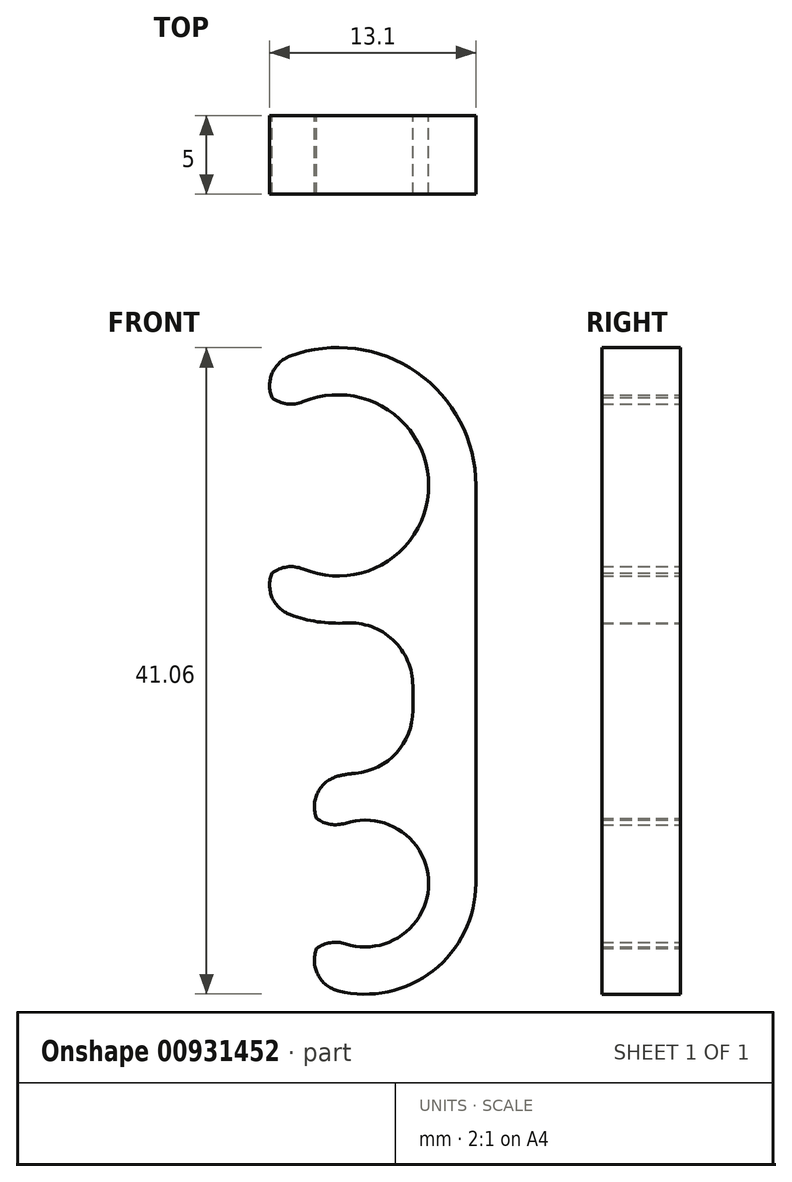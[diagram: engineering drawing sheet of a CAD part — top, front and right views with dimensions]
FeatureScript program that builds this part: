
annotation { "Feature Type Name" : "Feature", "Feature Type Description" : "" }
export const myFeature = defineFeature(function(context is Context, id is Id, definition is map)
    precondition{}
    {
        {
            var Q0;
            Q0=qCreatedBy(makeId("Front.planeOp"),FACE);
            var sketch = newSketch(context, id + "F0", { "sketchPlane" : qUnion([Q0])});
            skPoint(sketch, "E0", {"position": v(5.76, 0) * mm});
            skPoint(sketch, "E1", {"position": v(5.76, -25.29) * mm});
            skLineSegment(sketch, "E2", {"start": v(8.75, 0) * mm, "end": v(8.75, -25.29) * mm});
            skArc(sketch, "E3", {"start": v(-3.18, -8.16) * mm, "mid": v(-1.36, -8.65) * mm, "end": v(0.52, -8.74) * mm});
            skArc(sketch, "E4", {"start": v(-0.29, 8.75) * mm, "mid": v(-8.63, 1.48) * mm, "end": v(-3.18, -8.16) * mm});
            skArc(sketch, "E5", {"start": v(-2.55, -19.7) * mm, "mid": v(-5, -27.33) * mm, "end": v(1.27, -32.3) * mm});
            skArc(sketch, "E6", {"start": v(1.27, -32.3) * mm, "mid": v(8.53, -27.06) * mm, "end": v(4.75, -18.94) * mm});
            skLineSegment(sketch, "E7", {"start": v(-5.33, -6.95) * mm, "end": v(0, 0) * mm});
            skLineSegment(sketch, "E8", {"start": v(0, 0) * mm, "end": v(-5.33, 6.95) * mm});
            skLineSegment(sketch, "E9", {"start": v(1.73, -25.29) * mm, "end": v(-2.55, -19.7) * mm});
            skLineSegment(sketch, "E10", {"start": v(1.73, -25.29) * mm, "end": v(-2.55, -30.86) * mm});
            skArc(sketch, "E11", {"start": v(-3.5, 4.57) * mm, "mid": v(-5.76, 0) * mm, "end": v(-3.5, -4.57) * mm});
            skArc(sketch, "E12", {"start": v(-3.5, -4.57) * mm, "mid": v(5.76, 0) * mm, "end": v(-3.5, 4.57) * mm});
            skArc(sketch, "E13", {"start": v(-0.73, -22.09) * mm, "mid": v(-2.3, -25.29) * mm, "end": v(-0.73, -28.48) * mm});
            skArc(sketch, "E14", {"start": v(-0.73, -28.48) * mm, "mid": v(5.76, -25.29) * mm, "end": v(-0.73, -22.09) * mm});
            skLineSegment(sketch, "E15", {"start": v(1.73, -21.26) * mm, "end": v(-24.2, -21.26) * mm, "construction": true});
            skLineSegment(sketch, "E16", {"start": v(0, -5.75) * mm, "end": v(-23.66, -5.76) * mm, "construction": true});
            skLineSegment(sketch, "E17", {"start": v(4.75, -14.3) * mm, "end": v(4.75, -12.73) * mm});
            skArc(sketch, "E18", {"start": v(1.1, -18.28) * mm, "mid": v(-0.83, -18.73) * mm, "end": v(-2.55, -19.7) * mm});
            skArc(sketch, "E19", {"start": v(4.75, -7.35) * mm, "mid": v(8.35, 2.62) * mm, "end": v(-0.29, 8.75) * mm});
            skPoint(sketch, "E20.visualSharp", {"position": v(4.75, -7.35) * mm});
            skArc(sketch, "E20.filletArc", {"start": v(4.75, -12.73) * mm, "mid": v(3.5, -9.82) * mm, "end": v(0.52, -8.74) * mm});
            skPoint(sketch, "E21.visualSharp", {"position": v(4.75, -18.94) * mm});
            skArc(sketch, "E21.filletArc", {"start": v(1.1, -18.28) * mm, "mid": v(3.7, -17) * mm, "end": v(4.75, -14.3) * mm});
            skSolve(sketch);
        }
        {
            var Q0;
            {var subQ2=sQuery(id+"F0.wireOp",EDGE,"E2");Q0=makeQuery(id+"F0.imprint","IMPRINT",FACE,{"disambiguationData":[TD([[makeQuery(id+"F0.imprint","IMPRINT",EDGE,{"derivedFrom":subQ2}),-1.0]])]});}
            extrude(context, id + "F1", {"entities" : qUnion([Q0]), "depth" : 5 * mm, "offsetDistance" : 25 * mm});
        }
        {
            var Q0;
            Q0=makeQuery(id+"F1.opExtrude","SWEPT_EDGE",EDGE,{"disambiguationData":[OSD([sQuery(id+"F0.wireOp",EDGE,"E4"),sQuery(id+"F0.wireOp",EDGE,"E8")])]});
            var Q1;
            Q1=makeQuery(id+"F1.opExtrude","SWEPT_EDGE",EDGE,{"disambiguationData":[OSD([sQuery(id+"F0.wireOp",EDGE,"E8"),sQuery(id+"F0.wireOp",EDGE,"E11"),sQuery(id+"F0.wireOp",EDGE,"E12")])]});
            var Q2;
            Q2=makeQuery(id+"F1.opExtrude","SWEPT_EDGE",EDGE,{"disambiguationData":[OSD([sQuery(id+"F0.wireOp",EDGE,"E7"),sQuery(id+"F0.wireOp",EDGE,"E11"),sQuery(id+"F0.wireOp",EDGE,"E12")])]});
            var Q3;
            Q3=makeQuery(id+"F1.opExtrude","SWEPT_EDGE",EDGE,{"disambiguationData":[OSD([sQuery(id+"F0.wireOp",EDGE,"E4"),sQuery(id+"F0.wireOp",EDGE,"E7")])]});
            var Q4;
            Q4=makeQuery(id+"F1.opExtrude","SWEPT_EDGE",EDGE,{"disambiguationData":[OSD([sQuery(id+"F0.wireOp",EDGE,"E5"),sQuery(id+"F0.wireOp",EDGE,"680ca464-2a6f-4f87-88b0-3cb272eb12a2.filletArc")])]});
            var Q5;
            Q5=makeQuery(id+"F1.opExtrude","SWEPT_EDGE",EDGE,{"disambiguationData":[OSD([sQuery(id+"F0.wireOp",EDGE,"E9"),sQuery(id+"F0.wireOp",EDGE,"E13"),sQuery(id+"F0.wireOp",EDGE,"E14")])]});
            var Q6;
            Q6=makeQuery(id+"F1.opExtrude","SWEPT_EDGE",EDGE,{"disambiguationData":[OSD([sQuery(id+"F0.wireOp",EDGE,"E10"),sQuery(id+"F0.wireOp",EDGE,"E13"),sQuery(id+"F0.wireOp",EDGE,"E14")])]});
            var Q7;
            Q7=makeQuery(id+"F1.opExtrude","SWEPT_EDGE",EDGE,{"disambiguationData":[OSD([sQuery(id+"F0.wireOp",EDGE,"E5"),sQuery(id+"F0.wireOp",EDGE,"E10")])]});
            var Q8;
            Q8=makeQuery(id+"F1.opExtrude","SWEPT_EDGE",EDGE,{"disambiguationData":[OSD([sQuery(id+"F0.wireOp",EDGE,"E5"),sQuery(id+"F0.wireOp",EDGE,"E9"),sQuery(id+"F0.wireOp",EDGE,"E18")])]});
            fillet(context, id + "F2", {"entities" : qUnion([Q0, Q1, Q2, Q3, Q4, Q5, Q6, Q7, Q8]), "radius" : 2 * mm, "tangentPropagation" : true, "allowEdgeOverflow" : false});
        }
    });
